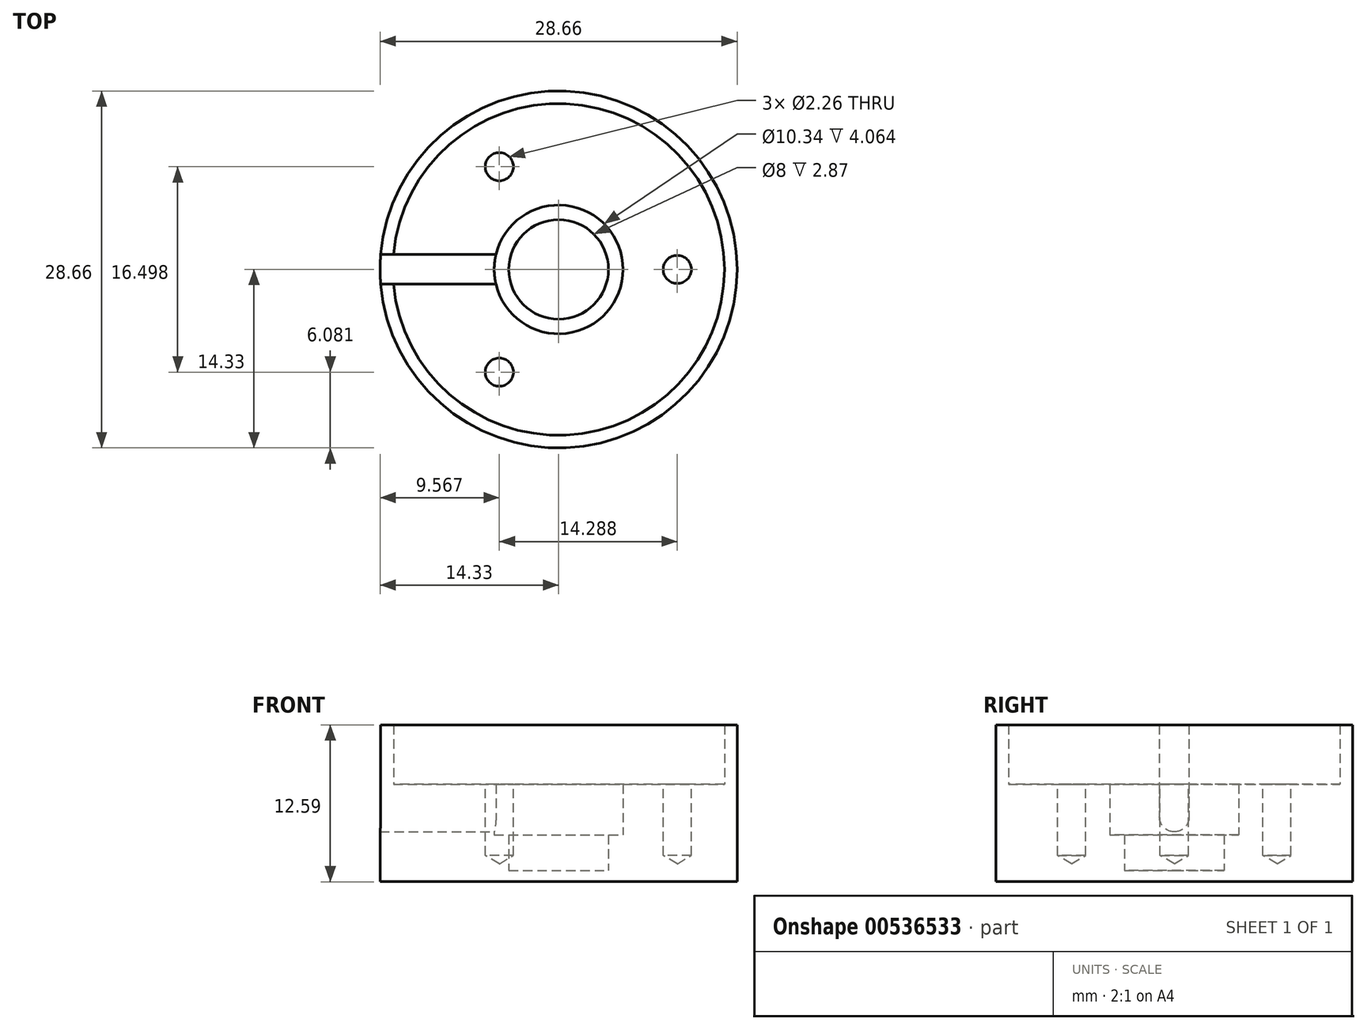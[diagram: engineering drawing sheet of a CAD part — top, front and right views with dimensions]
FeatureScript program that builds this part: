
annotation { "Feature Type Name" : "Feature", "Feature Type Description" : "" }
export const myFeature = defineFeature(function(context is Context, id is Id, definition is map)
    precondition{}
    {
        {
            var Q0;
            Q0=qCreatedBy(makeId("Front.planeOp"),FACE);
            var sketch = newSketch(context, id + "F0", { "sketchPlane" : qUnion([Q0])});
            skLineSegment(sketch, "E0", {"start": v(14.33, 0) * mm, "end": v(14.33, -12.59) * mm});
            skLineSegment(sketch, "E1", {"start": v(14.33, -12.59) * mm, "end": v(0, -12.59) * mm});
            skLineSegment(sketch, "E2", {"start": v(0, -12.59) * mm, "end": v(0, -11.7) * mm});
            skLineSegment(sketch, "E3", {"start": v(5.17, -4.76) * mm, "end": v(13.31, -4.76) * mm});
            skLineSegment(sketch, "E4", {"start": v(13.31, -4.76) * mm, "end": v(13.31, 0) * mm});
            skLineSegment(sketch, "E5", {"start": v(13.31, 0) * mm, "end": v(14.33, 0) * mm});
            skLineSegment(sketch, "E6", {"start": v(0, -11.7) * mm, "end": v(4, -11.7) * mm});
            skLineSegment(sketch, "E7", {"start": v(4, -11.7) * mm, "end": v(4, -8.83) * mm});
            skLineSegment(sketch, "E8", {"start": v(4, -8.83) * mm, "end": v(5.17, -8.83) * mm});
            skLineSegment(sketch, "E9", {"start": v(5.17, -8.83) * mm, "end": v(5.17, -4.76) * mm});
            skLineSegment(sketch, "E10", {"start": v(0, -12.59) * mm, "end": v(0, -26.31) * mm, "construction": true});
            skSolve(sketch);
        }
        {
            var Q0;
            Q0=qSketchRegion(id+"F0",true);
            var Q1;
            Q1=sQuery(id+"F0.wireOp",EDGE,"E2");
            revolve(context, id + "F1", {"entities" : qUnion([Q0]), "axis" : qUnion([Q1]), "revolveType" : RevolveType.FULL});
        }
        {
            var Q0;
            Q0=qCreatedBy(makeId("Right.planeOp"),FACE);
            var sketch = newSketch(context, id + "F2", { "sketchPlane" : qUnion([Q0])});
            skLineSegment(sketch, "E11", {"start": v(-1.2, -7.38) * mm, "end": v(-1.2, 0) * mm});
            skLineSegment(sketch, "E12", {"start": v(-1.2, 0) * mm, "end": v(1.2, 0) * mm});
            skLineSegment(sketch, "E13", {"start": v(1.2, 0) * mm, "end": v(1.2, -7.38) * mm});
            skArc(sketch, "E14", {"start": v(1.2, -7.38) * mm, "mid": v(0, -8.57) * mm, "end": v(-1.2, -7.38) * mm});
            skSolve(sketch);
        }
        {
            var Q0;
            Q0 = qSketchRegion(id + "F2", true);
            extrude(context, id + "F3", {"entities" : qUnion([Q0]), "operationType" : NewBodyOperationType.REMOVE, "oppositeDirection" : true, "depth" : 25.4 * mm, "offsetDistance" : 25.4 * mm});
        }
        {
            var Q0;
            Q0=makeQuery(id+"F1.opRevolve","SWEPT_FACE",FACE,{"disambiguationData":[OSD([sQuery(id+"F0.wireOp",EDGE,"E3")])]});
            var sketch = newSketch(context, id + "F4", { "sketchPlane" : qUnion([Q0])});
            skPoint(sketch, "E15", {"position": v(9.52, 0) * mm});
            skPoint(sketch, "E16.1.0", {"position": v(-4.76, 8.25) * mm});
            skPoint(sketch, "E16.2.0", {"position": v(-4.76, -8.25) * mm});
            skPoint(sketch, "E16.center", {"position": v(0, 0) * mm});
            skSolve(sketch);
        }
        {
            var Q0;
            Q0=sQuery(id+"F4.wireOp",VERTEX,"E15");
            var Q1;
            Q1=sQuery(id+"F4.wireOp",VERTEX,"E16.1.0");
            var Q2;
            Q2=sQuery(id+"F4.wireOp",VERTEX,"E16.2.0");
            var Q3;
            Q3=makeQuery(id+"F1.opRevolve","SWEPT_BODY",BODY,{"disambiguationData":[OSD([sQuery(id+"F0.wireOp",EDGE,"E0"),sQuery(id+"F0.wireOp",EDGE,"E1"),sQuery(id+"F0.wireOp",EDGE,"E2"),sQuery(id+"F0.wireOp",EDGE,"E3"),sQuery(id+"F0.wireOp",EDGE,"E4"),sQuery(id+"F0.wireOp",EDGE,"E5"),sQuery(id+"F0.wireOp",EDGE,"E6"),sQuery(id+"F0.wireOp",EDGE,"E7"),sQuery(id+"F0.wireOp",EDGE,"E8"),sQuery(id+"F0.wireOp",EDGE,"E9")])]});
            hole(context, id + "F5", {"style" : HoleStyle.SIMPLE, "endStyle" : HoleEndStyle.BLIND, "standardTappedOrClearance" : lookupTablePath({ "standard" : "ANSI", "engagement" : "75%", "pitch" : "40 tpi", "size" : "#4", "type" : "Tapped" }), "standardBlindInLast" : lookupTablePath({ "standard" : "ANSI", "engagement" : "75%", "pitch" : "40 tpi", "size" : "#4", "type" : "Tapped" }), "holeDiameter" : 2.26 * mm, "majorDiameter" : 2.84 * mm, "showTappedDepth" : true, "holeDepth" : 5.72 * mm, "tappedDepth" : 5.08 * mm, "tapClearance" : 1, "startFromSketch" : true, "locations" : qUnion([Q0, Q1, Q2]), "scope" : qUnion([Q3])});
        }
    });
